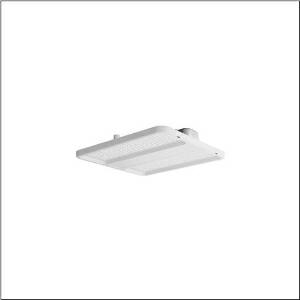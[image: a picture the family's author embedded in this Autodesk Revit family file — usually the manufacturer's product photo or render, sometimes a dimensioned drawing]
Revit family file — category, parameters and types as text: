
# Revit family: highbay_21_midi_52hn11da4hda
name_source: partatom
category: Lighting Fixtures
units: mm (PartAtom-declared; Revit-internal decimal feet)

## family parameters
Cut with Voids When Loaded = No
Host = Face
Light Source = No
Part Type = Normal
Room Calculation Point = No
Round Connector Dimension = Use Diameter
Shared = No

## types (1)
- --- (1 x LED, 2910 lm, 15.9 W, 4000K)
    Apparent Load = 16 VA
    CIE Flux Codes = 89 97 99 100 100
    Color Rendering = 80
    Color Temperature = 4000K
    Default Elevation = 1800 mm
    Description = high bay luminaire Highbay 21 midi; direct symmetric narrow distribution, light control with lens of PMMA; UGR ≤ 22 (X = 4H | Y = 8H | S = 0.25H | reflection values 70/50/20); luminous flux: 19.000lm; light colour: 840, colour temperature: 4000K, MacAdam ≤ 3 SDCM (initial), colour rendering: CRI > 80; luminous efficacy: 192,1lm/W; rated service life: 75.000h (L80/B50) at AT= ta max; control: DALI 2; housing frame of high-performance plastic PA6, matt traffic white (RAL 9016); cover of PMMA; dimension (LxWxH): 474 x 442 x 72mm; luminaire connection: terminal, 5-pole, max. 2.5mm² (cable entry for one cable, Ø 8.5..16mm); mains connection: 230..240V, AC/DC 0/50..60Hz; connected load: 98,9W; protection rating (complete): IP66; insulation class (complete): insulation class I (protective earthing); protection symbol: D; impact resistance: IK08; halogen-free wiring; for central battery installations according to DIN EN 60598-2-22; LABS conformity tested according to VDMA 24364:2018-05; corresponds to IFS (International Featured Standards) requirements for safety and quality in the food industry; certification: CE, ENEC, VDE, UKCA; permissible operating ambient temperature: -40..+60°C (reducing of maximum allowable ambient temperature of 5°C with ceiling mounting); packaging unit: 1 piece; (delivery without accessories; please order mounting accessories separately)
    Height = 72 mm  [stored 0.23622 ft]
    Lamp = 1 x LED
    Lamp Light Flux = 2910 lm
    Lamp Power = 15.9 W
    Lamp count = 1
    Length = 474 mm
    Luminous efficacy = 183 lm/W
    Manufacturer = Siteco
    ModVariant = No
    Model = 52HN11DA4HDA
    Mounting Place = Ceiling
    Mounting Type = Pendant
    Number of Poles = 1
    OnlyDefault = Yes
    Power Factor = 1
    Product Name = Highbay 21 midi
    Product group = high bay luminaire
    ProductGroupID = 901
    Protection Class = Protection class I
    Protection Degree = IP 66
    RLX_Detail_Level = 1
    RLX_Emergency_Light_Flux = 0 lm
    RLX_Emergency_Type = 0
    RLX_Emergency_Type_DB = No
    RlxData = <blob elided: 17577 chars, md5=dbf0429f>
    Socket = socket
    Standby Power = 0 W
    System Light Flux = 2910 lm
    System Power = 16 W
    Type Comments = : DC mode (central or group accumulator) initial emergency light level
    Type Image = l_1363240.jpg
    URL = http://relux.com
    VarID = @adj_000177
    Voltage = 0 V
    Weight = 0.00 kg
    Width = 442 mm

note: [stored X ft] marks values corroborated as IEEE doubles in the binary element streams (Revit-internal decimal feet)

## geometry (parser evidence)
native form markers: Blend x4, Sweep x11
no freeform markers — native parametric forms only
